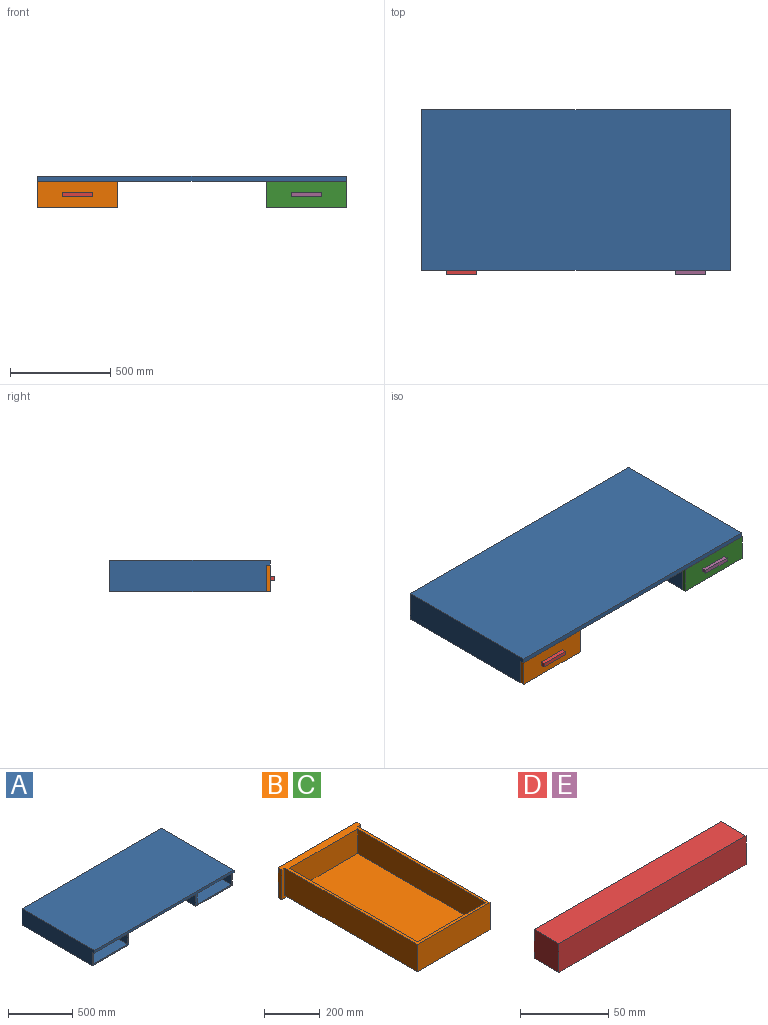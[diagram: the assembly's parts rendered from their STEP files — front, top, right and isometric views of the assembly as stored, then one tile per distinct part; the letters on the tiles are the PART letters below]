
ASSEMBLY  parts=5 mates=4
PART A: 20 faces, bbox 1540x800x156 mm
  f0: plane 1540x800mm, normal (0,0,-1), area 1185536mm2, adj f1,f3,f5,f6,f7,f8,f9,f10
  f1: plane 768x120mm, normal (-1,0,0), area 92160mm2, adj f0,f2,f17,f19
  f2: plane 768x376mm, normal (0,0,1), area 288768mm2, adj f1,f7,f17,f19
  f3: plane 768x120mm, normal (1,0,0), area 92160mm2, adj f0,f4,f16,f18
  f4: plane 768x376mm, normal (0,0,1), area 288768mm2, adj f3,f8,f16,f18
  f5: plane 800x156mm, normal (1,0,0), area 122160mm2, adj f0,f6,f9,f11,f15,f16
  f6: plane 1540x24mm, normal (0,-1,0), area 36960mm2, adj f0,f5,f10,f11
  f7: plane 768x120mm, normal (1,0,0), area 92160mm2, adj f0,f2,f17,f19
  f8: plane 768x120mm, normal (-1,0,0), area 92160mm2, adj f0,f4,f16,f18
  f9: plane 1540x156mm, normal (0,1,0), area 142560mm2, adj f0,f5,f10,f11,f12,f13,f14,f15
  f10: plane 800x156mm, normal (-1,0,0), area 122160mm2, adj f0,f6,f9,f11,f14,f17
  f11: plane 1540x800mm, normal (0,0,1), area 1232000mm2, adj f5,f6,f9,f10
  f12: plane 780x132mm, normal (1,0,0), area 102960mm2, adj f0,f9,f14,f17
  f13: plane 780x132mm, normal (-1,0,0), area 102960mm2, adj f0,f9,f15,f16
  f14: plane 780x400mm, normal (0,0,-1), area 312000mm2, adj f9,f10,f12,f17
  f15: plane 780x400mm, normal (0,0,-1), area 312000mm2, adj f5,f9,f13,f16
  f16: plane 400x132mm, normal (0,-1,0), area 7680mm2, adj f0,f3,f4,f5,f8,f13,f15
  f17: plane 400x132mm, normal (0,-1,0), area 7680mm2, adj f0,f1,f2,f7,f10,f12,f14
  f18: plane 376x120mm, normal (0,-1,0), area 45120mm2, adj f0,f3,f4,f8
  f19: plane 376x120mm, normal (0,-1,0), area 45120mm2, adj f0,f1,f2,f7
PART B: 20 faces, bbox 400x694x132 mm
  f0: plane 346x108mm, normal (0,-1,0), area 37368mm2, adj f4,f9,f10,f11
  f1: plane 346x6mm, normal (0,-1,0), area 2076mm2, adj f2,f6,f7,f8
  f2: plane 674x370mm, normal (0,0,-1), area 24480mm2, adj f1,f3,f5,f6,f8,f12,f13,f15
  f3: plane 674x120mm, normal (1,0,0), area 80880mm2, adj f2,f4,f13,f15
  f4: plane 694x400mm, normal (0,0,1), area 32480mm2, adj f0,f3,f5,f9,f11,f13,f14,f15
  f5: plane 674x120mm, normal (-1,0,0), area 80880mm2, adj f2,f4,f13,f15
  f6: plane 650x6mm, normal (1,0,0), area 3900mm2, adj f1,f2,f7,f12
  f7: plane 650x346mm, normal (0,0,-1), area 224900mm2, adj f1,f6,f8,f12
  f8: plane 650x6mm, normal (-1,0,0), area 3900mm2, adj f1,f2,f7,f12
  f9: plane 650x108mm, normal (-1,0,0), area 70200mm2, adj f0,f4,f10,f14
  f10: plane 650x346mm, normal (0,0,1), area 224900mm2, adj f0,f9,f11,f14
  f11: plane 650x108mm, normal (1,0,0), area 70200mm2, adj f0,f4,f10,f14
  f12: plane 346x6mm, normal (0,1,0), area 2076mm2, adj f2,f6,f7,f8
  f13: plane 370x120mm, normal (0,-1,0), area 44400mm2, adj f2,f3,f4,f5
  f14: plane 346x108mm, normal (0,1,0), area 37368mm2, adj f4,f9,f10,f11
  f15: plane 400x132mm, normal (0,-1,0), area 8400mm2, adj f2,f3,f4,f5,f16,f17,f18
  f16: plane 132x20mm, normal (1,0,0), area 2640mm2, adj f4,f15,f17,f19
  f17: plane 400x20mm, normal (0,0,-1), area 8000mm2, adj f15,f16,f18,f19
  f18: plane 132x20mm, normal (-1,0,0), area 2640mm2, adj f4,f15,f17,f19
  f19: plane 400x132mm, normal (0,1,0), area 52800mm2, adj f4,f16,f17,f18
PART C: same geometry as B
PART D: 6 faces, bbox 150x20x20 mm
  f0: plane 150x20mm, normal (0,0,-1), area 3000mm2, adj f1,f3,f4,f5
  f1: plane 20x20mm, normal (-1,0,0), area 400mm2, adj f0,f2,f4,f5
  f2: plane 150x20mm, normal (0,0,1), area 3000mm2, adj f1,f3,f4,f5
  f3: plane 20x20mm, normal (1,0,0), area 400mm2, adj f0,f2,f4,f5
  f4: plane 150x20mm, normal (0,1,0), area 3000mm2, adj f0,f1,f2,f3
  f5: plane 150x20mm, normal (0,-1,0), area 3000mm2, adj f0,f1,f2,f3
PART E: same geometry as D
PLACE A t=(-143.95,-45.28,138.36)mm fixed
PLACE B rot(axis=(0,0,1),180deg) t=(-898.95,-425.28,18.36)mm
PLACE C rot(axis=(0,0,1),180deg) t=(241.05,-425.28,18.36)mm
PLACE D t=(-528.95,-485.28,18.36)mm
PLACE E t=(611.05,-485.28,18.36)mm
MATE fastened E.f4 <-> C.f19  axis (0,1,0) through (426.05,-445.28,72.36)mm
MATE slider B.f15 <-> A.f17  axis (0,1,0) through (-713.95,-425.28,18.36)mm
MATE slider C.f15 <-> A.f16  axis (0,1,0) through (426.05,-425.28,18.36)mm
MATE fastened D.f4 <-> B.f19  axis (0,1,0) through (-713.95,-445.28,72.36)mm
